# Revit family: Electrical-Box_FSR_PWB250
name_source: partatom
category: Generic Models
units: mm (PartAtom-declared; Revit-internal decimal feet)

## family parameters
Can host rebar = No
Classification Number = 23.80.50.00
Cut with Voids When Loaded = No
Host = Face
Maintain Annotation Orientation = No
Part Type = Normal
Room Calculation Point = No
Round Connector Dimension = Use Diameter
Shared = No

## types (4) — shared parameters
Assembly Code = D5020100
Construction Details = http://www.arcat.com
Default Elevation = 0' - 0"
Green Building-LEED = http://www.arcat.com
Installation-Fabrication = ftp://doclib.fsrinc.com/
Keynote = 26 27 26
Manufacturer = FSR, Inc
Manufacturer Fax = 973-785-4207
Manufacturer Website = http://fsrinc.com
Product Data = http://www.arcat.com
Revision = R1_2016-06
Sales Information = http://fsrinc.com
Specification = http://www.arcat.com
Standards Conformance = UL  ;  CSA C22.2
Test Data = ftp://doclib.fsrinc.com/
URL = http://fsrinc.com
Unit Height = 0' - 7 1/2"
Unit Width = 1' - 2 3/4"
zero-valued in all types: Cost, Expected Lifespan (Years), Maintenance Schedule (Months), Warranty Duration (Years)

## per-type parameters (varying)
| type | Cover Finish | Description | Model | Unit Depth |
| 3in Deep Box Black | Metal - Aluminum - Painted Black | FSR Video Display Wall Box - PWB-253-BLK as Specified | PWB-253-BLK | 0' - 2 7/8" |
| 3in Deep Box White | Metal - Aluminum - Painted White | FSR Video Display Wall Box - PWB-253-WHT as Specified | PWB-253-WHT | 0' - 2 7/8" |
| 4in Deep Box Black | Metal - Aluminum - Painted Black | FSR Video Display Wall Box - PWB-250-BLK as Specified | PWB-250-BLK | 0' - 4" |
| 4in Deep Box White | Metal - Aluminum - Painted White | FSR Video Display Wall Box - PWB-250-WHT as Specified | PWB-250-WHT | 0' - 4" |

## geometry (parser evidence)
native form markers: Sweep x2
no freeform markers — native parametric forms only
